annotation { "Feature Type Name" : "Feature", "Feature Type Description" : "" }
export const myFeature = defineFeature(function(context is Context, id is Id, definition is map)
    precondition{}
    {
        {
            var Q0;
            Q0=qCreatedBy(makeId("Front.planeOp"),FACE);
            var sketch = newSketch(context, id + "F0", { "sketchPlane" : qUnion([Q0])});
            skLineSegment(sketch, "E0", {"start": v(-68.86, 30) * mm, "end": v(38.78, 5) * mm});
            skLineSegment(sketch, "E1", {"start": v(-68.86, 30) * mm, "end": v(-63.42, 15.03) * mm});
            skLineSegment(sketch, "E2", {"start": v(-63.42, 15.03) * mm, "end": v(-68.66, 0) * mm});
            skLineSegment(sketch, "E3", {"start": v(-60.3, 0) * mm, "end": v(-59.2, 1.1) * mm});
            skLineSegment(sketch, "E4", {"start": v(-59.2, 1.1) * mm, "end": v(-58.12, 0) * mm});
            skLineSegment(sketch, "E5", {"start": v(-68.66, 0) * mm, "end": v(-60.3, 0) * mm});
            skLineSegment(sketch, "E6", {"start": v(-58.12, 0) * mm, "end": v(-57.03, -1.1) * mm});
            skLineSegment(sketch, "E7", {"start": v(-57.03, -1.1) * mm, "end": v(-55.05, 1.1) * mm});
            skLineSegment(sketch, "E8", {"start": v(-55.05, 1.1) * mm, "end": v(-53.07, -1.1) * mm});
            skLineSegment(sketch, "E9", {"start": v(-60.55, 1.1) * mm, "end": v(-52.83, 1.1) * mm, "construction": true});
            skLineSegment(sketch, "E10.1.0.0", {"start": v(-53.09, -1.09) * mm, "end": v(-51.1, 1.1) * mm});
            skLineSegment(sketch, "E10.1.0.1", {"start": v(-51.1, 1.1) * mm, "end": v(-49.13, -1.09) * mm});
            skLineSegment(sketch, "E10.2.0.0", {"start": v(-49.15, -1.09) * mm, "end": v(-47.17, 1.1) * mm});
            skLineSegment(sketch, "E10.2.0.1", {"start": v(-47.17, 1.1) * mm, "end": v(-45.2, -1.09) * mm});
            skLineSegment(sketch, "E10.direction1", {"start": v(-57.03, -1.1) * mm, "end": v(-53.09, -1.09) * mm, "construction": true});
            skLineSegment(sketch, "E11.0.3.0", {"start": v(-45.21, -1.08) * mm, "end": v(-43.23, 1.1) * mm});
            skLineSegment(sketch, "E11.3.3.0", {"start": v(-43.23, 1.1) * mm, "end": v(-41.26, -1.08) * mm});
            skLineSegment(sketch, "E11.0.4.0", {"start": v(-41.28, -1.08) * mm, "end": v(-39.3, 1.1) * mm});
            skLineSegment(sketch, "E11.3.4.0", {"start": v(-39.3, 1.1) * mm, "end": v(-37.32, -1.08) * mm});
            skLineSegment(sketch, "E11.0.5.0", {"start": v(-37.34, -1.08) * mm, "end": v(-35.36, 1.1) * mm});
            skLineSegment(sketch, "E11.3.5.0", {"start": v(-35.36, 1.1) * mm, "end": v(-33.38, -1.08) * mm});
            skLineSegment(sketch, "E11.0.6.0", {"start": v(-33.4, -1.07) * mm, "end": v(-31.42, 1.1) * mm});
            skLineSegment(sketch, "E11.3.6.0", {"start": v(-31.42, 1.1) * mm, "end": v(-29.44, -1.07) * mm});
            skLineSegment(sketch, "E11.0.7.0", {"start": v(-29.47, -1.07) * mm, "end": v(-27.49, 1.11) * mm});
            skLineSegment(sketch, "E11.3.7.0", {"start": v(-27.49, 1.11) * mm, "end": v(-25.5, -1.07) * mm});
            skLineSegment(sketch, "E11.0.8.0", {"start": v(-25.53, -1.07) * mm, "end": v(-23.55, 1.11) * mm});
            skLineSegment(sketch, "E11.3.8.0", {"start": v(-23.55, 1.11) * mm, "end": v(-21.57, -1.07) * mm});
            skLineSegment(sketch, "E11.0.9.0", {"start": v(-21.6, -1.07) * mm, "end": v(-19.61, 1.12) * mm});
            skLineSegment(sketch, "E11.3.9.0", {"start": v(-19.61, 1.12) * mm, "end": v(-17.63, -1.07) * mm});
            skLineSegment(sketch, "E11.0.10.0", {"start": v(-17.65, -1.06) * mm, "end": v(-15.67, 1.12) * mm});
            skLineSegment(sketch, "E11.3.10.0", {"start": v(-15.67, 1.12) * mm, "end": v(-13.7, -1.06) * mm});
            skLineSegment(sketch, "E11.0.11.0", {"start": v(-13.72, -1.06) * mm, "end": v(-11.74, 1.12) * mm});
            skLineSegment(sketch, "E11.3.11.0", {"start": v(-11.74, 1.12) * mm, "end": v(-9.76, -1.06) * mm});
            skLineSegment(sketch, "E11.0.12.0", {"start": v(-9.78, -1.06) * mm, "end": v(-7.8, 1.12) * mm});
            skLineSegment(sketch, "E11.3.12.0", {"start": v(-7.8, 1.12) * mm, "end": v(-5.82, -1.06) * mm});
            skLineSegment(sketch, "E11.0.13.0", {"start": v(-5.84, -1.06) * mm, "end": v(-3.86, 1.13) * mm});
            skLineSegment(sketch, "E11.3.13.0", {"start": v(-3.86, 1.13) * mm, "end": v(-1.88, -1.06) * mm});
            skLineSegment(sketch, "E11.0.14.0", {"start": v(-1.9, -1.05) * mm, "end": v(0.07, 1.13) * mm});
            skLineSegment(sketch, "E11.3.14.0", {"start": v(0.07, 1.13) * mm, "end": v(2.05, -1.05) * mm});
            skLineSegment(sketch, "E11.0.15.0", {"start": v(2.03, -1.05) * mm, "end": v(4.01, 1.13) * mm});
            skLineSegment(sketch, "E11.3.15.0", {"start": v(4.01, 1.13) * mm, "end": v(6, -1.05) * mm});
            skLineSegment(sketch, "E11.0.16.0", {"start": v(5.97, -1.05) * mm, "end": v(7.95, 1.14) * mm});
            skLineSegment(sketch, "E11.3.16.0", {"start": v(7.95, 1.14) * mm, "end": v(9.93, -1.05) * mm});
            skLineSegment(sketch, "E11.0.17.0", {"start": v(9.9, -1.04) * mm, "end": v(11.89, 1.14) * mm});
            skLineSegment(sketch, "E11.3.17.0", {"start": v(11.89, 1.14) * mm, "end": v(13.87, -1.04) * mm});
            skLineSegment(sketch, "E11.0.18.0", {"start": v(13.84, -1.04) * mm, "end": v(15.82, 1.14) * mm});
            skLineSegment(sketch, "E11.3.18.0", {"start": v(15.82, 1.14) * mm, "end": v(17.8, -1.04) * mm});
            skLineSegment(sketch, "E11.0.19.0", {"start": v(17.78, -1.04) * mm, "end": v(19.76, 1.14) * mm});
            skLineSegment(sketch, "E11.3.19.0", {"start": v(19.76, 1.14) * mm, "end": v(21.74, -1.04) * mm});
            skLineSegment(sketch, "E11.0.20.0", {"start": v(21.72, -1.04) * mm, "end": v(23.7, 1.15) * mm});
            skLineSegment(sketch, "E11.3.20.0", {"start": v(23.7, 1.15) * mm, "end": v(25.68, -1.04) * mm});
            skLineSegment(sketch, "E11.0.21.0", {"start": v(25.65, -1.03) * mm, "end": v(27.63, 1.15) * mm});
            skLineSegment(sketch, "E11.3.21.0", {"start": v(27.63, 1.15) * mm, "end": v(29.61, -1.03) * mm});
            skLineSegment(sketch, "E12", {"start": v(30.6, 0) * mm, "end": v(35.36, 0) * mm});
            skLineSegment(sketch, "E13", {"start": v(38.78, 0) * mm, "end": v(35.36, 0) * mm});
            skPoint(sketch, "E14", {"position": v(38.78, 5) * mm});
            skPoint(sketch, "E14.positionSnap0", {"position": v(38.78, 0) * mm});
            skArc(sketch, "E15", {"start": v(38.78, 0) * mm, "mid": v(40.76, 2.5) * mm, "end": v(38.78, 5) * mm});
            skLineSegment(sketch, "E16", {"start": v(29.61, -1.03) * mm, "end": v(30.6, 0) * mm});
            skLineSegment(sketch, "E17", {"start": v(-68.86, 30) * mm, "end": v(-68.66, 0) * mm, "construction": true});
            skSolve(sketch);
        }
        {
            var Q0;
            Q0 = qSketchRegion(id + "F0", true);
            extrude(context, id + "F1", {"entities" : qUnion([Q0]), "oppositeDirection" : true, "depth" : 30 * mm});
        }
        {
            var Q0;
            Q0=makeQuery(id+"F1.opExtrude","CAP_EDGE",EDGE,{"disambiguationData":[OSD([sQuery(id+"F0.wireOp",EDGE,"E1")])],"isStart":false});
            var Q1;
            Q1=makeQuery(id+"F1.opExtrude","CAP_EDGE",EDGE,{"disambiguationData":[OSD([sQuery(id+"F0.wireOp",EDGE,"E2")])],"isStart":false});
            var Q2;
            Q2=makeQuery(id+"F1.opExtrude","CAP_EDGE",EDGE,{"disambiguationData":[OSD([sQuery(id+"F0.wireOp",EDGE,"E2")])],"isStart":true});
            var Q3;
            Q3=makeQuery(id+"F1.opExtrude","CAP_EDGE",EDGE,{"disambiguationData":[OSD([sQuery(id+"F0.wireOp",EDGE,"E1")])],"isStart":true});
            chamfer(context, id + "F2", {"entities" : qUnion([Q0, Q1, Q2, Q3]), "width" : 2 * mm, "tangentPropagation" : true});
        }
        {
            var Q0;
            Q0=qCreatedBy(makeId("Front.planeOp"),FACE);
            var sketch = newSketch(context, id + "F3", { "sketchPlane" : qUnion([Q0])});
            skText(sketch, "E18", { "text": "Chihuahua Studios", "fontName": "AllertaStencil-Regular.ttf"});
            const initialGuessF3  = {"E18": [-0.06263, 0.0025, 1, 0, 0.007]};
            skSetInitialGuess(sketch, initialGuessF3);
            skSolve(sketch);
        }
        {
            var Q0;
            Q0 = qSketchRegion(id + "F3", true);
            extrude(context, id + "F4", {"entities" : qUnion([Q0]), "operationType" : NewBodyOperationType.REMOVE, "oppositeDirection" : true, "depth" : .75 * mm});
        }
    });